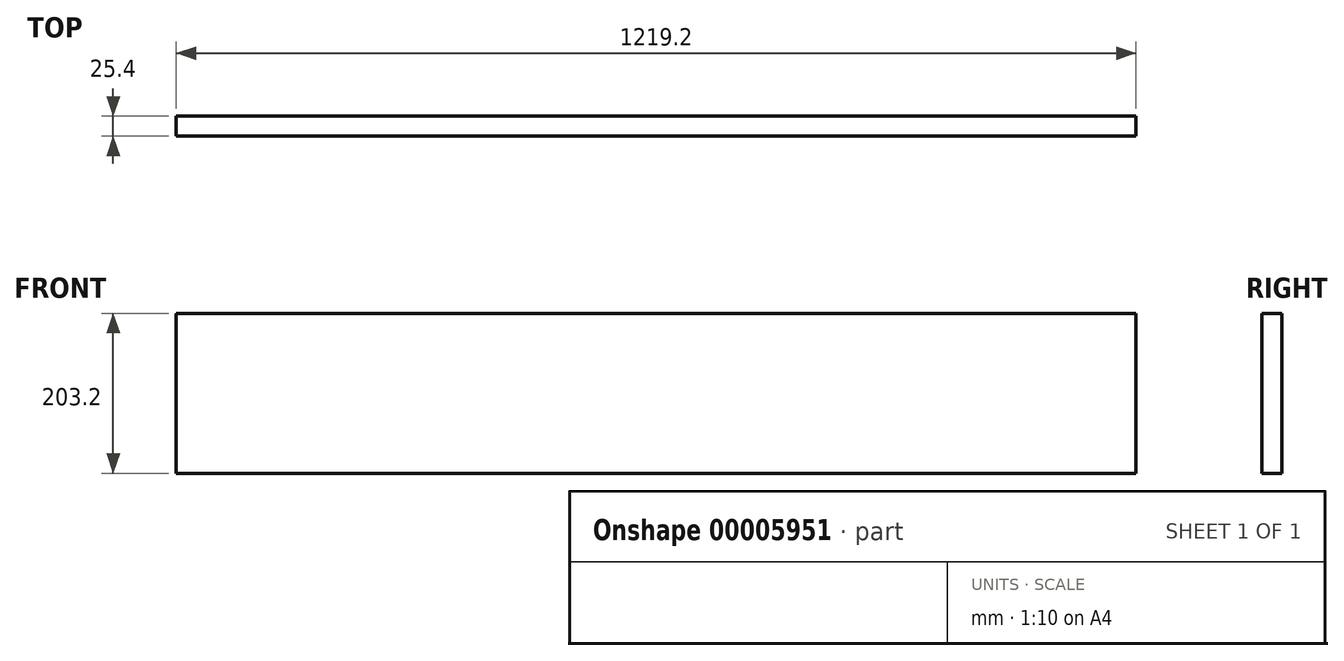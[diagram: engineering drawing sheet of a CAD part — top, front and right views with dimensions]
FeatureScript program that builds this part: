
annotation { "Feature Type Name" : "Feature", "Feature Type Description" : "" }
export const myFeature = defineFeature(function(context is Context, id is Id, definition is map)
    precondition{}
    {
        {
            var Q0;
            Q0=qCreatedBy(makeId("Front.planeOp"),FACE);
            var sketch = newSketch(context, id + "F0", { "sketchPlane" : qUnion([Q0])});
            skLineSegment(sketch, "E0.bottom", {"start": v(-598.41, 71.92) * mm, "end": v(620.79, 71.92) * mm});
            skLineSegment(sketch, "E0.top", {"start": v(-598.41, -131.28) * mm, "end": v(620.79, -131.28) * mm});
            skLineSegment(sketch, "E0.left", {"start": v(-598.41, 71.92) * mm, "end": v(-598.41, -131.28) * mm});
            skLineSegment(sketch, "E0.right", {"start": v(620.79, 71.92) * mm, "end": v(620.79, -131.28) * mm});
            skSolve(sketch);
        }
        {
            var Q0;
            Q0=makeQuery(id+"F0.imprint","IMPRINT",FACE,{"disambiguationData":[TD([[makeQuery(id+"F0.imprint","IMPRINT",EDGE,{"derivedFrom":sQuery(id+"F0.wireOp",EDGE,"E0.bottom")}),-1.0]])]});
            extrude(context, id + "F1", {"entities" : qUnion([Q0]), "depth" : 25.4 * mm});
        }
    });
